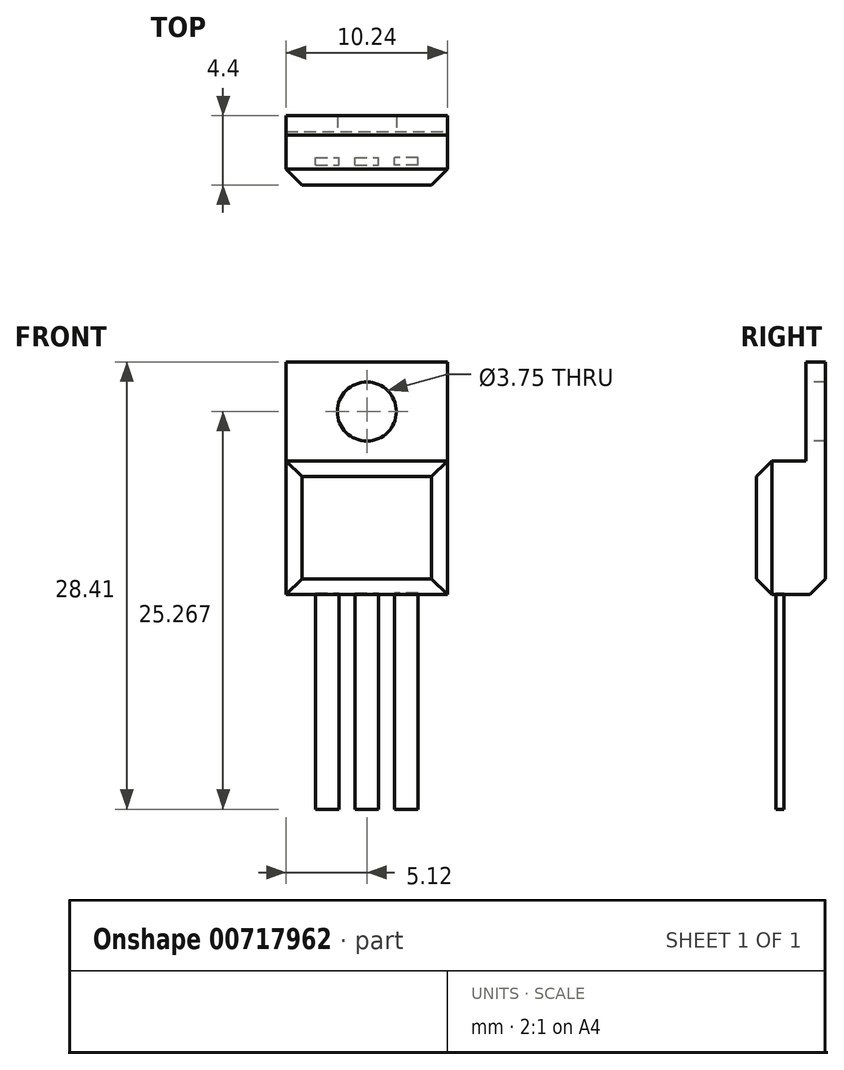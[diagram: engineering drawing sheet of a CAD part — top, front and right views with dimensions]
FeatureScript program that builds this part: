
annotation { "Feature Type Name" : "Feature", "Feature Type Description" : "" }
export const myFeature = defineFeature(function(context is Context, id is Id, definition is map)
    precondition{}
    {
        {
            var Q0;
            Q0=qCreatedBy(makeId("Front.planeOp"),FACE);
            var sketch = newSketch(context, id + "F0", { "sketchPlane" : qUnion([Q0])});
            skLineSegment(sketch, "E0.bottom", {"start": v(-5.12, 4.25) * mm, "end": v(5.12, 4.25) * mm});
            skLineSegment(sketch, "E0.top", {"start": v(-5.12, -4.25) * mm, "end": v(5.12, -4.25) * mm});
            skLineSegment(sketch, "E0.left", {"start": v(-5.12, 4.25) * mm, "end": v(-5.12, -4.25) * mm});
            skLineSegment(sketch, "E0.right", {"start": v(5.12, 4.25) * mm, "end": v(5.12, -4.25) * mm});
            skSolve(sketch);
        }
        {
            var Q0;
            Q0 = qSketchRegion(id + "F0", true);
            extrude(context, id + "F1", {"entities" : qUnion([Q0]), "depth" : 4.4 * mm, "offsetDistance" : 25 * mm});
        }
        {
            var Q0;
            Q0=qCreatedBy(makeId("Front.planeOp"),FACE);
            var sketch = newSketch(context, id + "F2", { "sketchPlane" : qUnion([Q0])});
            skLineSegment(sketch, "E1.bottom", {"start": v(-5.12, 4.12) * mm, "end": v(5.13, 4.13) * mm});
            skLineSegment(sketch, "E1.top", {"start": v(-5.12, 10.53) * mm, "end": v(5.12, 10.53) * mm});
            skLineSegment(sketch, "E1.left", {"start": v(-5.12, 4.12) * mm, "end": v(-5.12, 10.53) * mm});
            skLineSegment(sketch, "E1.right", {"start": v(5.13, 4.13) * mm, "end": v(5.12, 10.53) * mm});
            skSolve(sketch);
        }
        {
            var Q0;
            Q0=makeQuery(id+"F2.imprint","IMPRINT",FACE,{"disambiguationData":[TD([[makeQuery(id+"F2.imprint","IMPRINT",EDGE,{"derivedFrom":sQuery(id+"F2.wireOp",EDGE,"E1.bottom")}),1.0]])]});
            extrude(context, id + "F3", {"entities" : qUnion([Q0]), "operationType" : NewBodyOperationType.ADD, "depth" : 1.25 * mm, "offsetDistance" : 25 * mm});
        }
        {
            var Q0;
            Q0=makeQuery(id+"F3.opExtrude","CAP_FACE",FACE,{"disambiguationData":[OSD([sQuery(id+"F2.wireOp",EDGE,"E1.bottom"),sQuery(id+"F2.wireOp",EDGE,"E1.top"),sQuery(id+"F2.wireOp",EDGE,"E1.left"),sQuery(id+"F2.wireOp",EDGE,"E1.right")])],"isStart":false});
            var sketch = newSketch(context, id + "F4", { "sketchPlane" : qUnion([Q0])});
            skPoint(sketch, "E2", {"position": v(0, 7.39) * mm});
            skPoint(sketch, "E2.positionSnap0", {"position": v(5.12, 7.39) * mm});
            skPoint(sketch, "E2.positionSnap1", {"position": v(0, 10.53) * mm});
            skSolve(sketch);
        }
        {
            var Q0;
            Q0=sQuery(id+"F4.wireOp",VERTEX,"E2");
            var Q1;
            Q1=makeQuery(id+"F1.opExtrude","SWEPT_BODY",BODY,{"disambiguationData":[OSD([sQuery(id+"F0.wireOp",EDGE,"E0.bottom"),sQuery(id+"F0.wireOp",EDGE,"E0.top"),sQuery(id+"F0.wireOp",EDGE,"E0.left"),sQuery(id+"F0.wireOp",EDGE,"E0.right")])]});
            hole(context, id + "F5", {"style" : HoleStyle.SIMPLE, "endStyle" : HoleEndStyle.THROUGH, "holeDiameter" : 3.75 * mm, "majorDiameter" : 5 * mm, "isTappedThrough" : true, "tappedDepth" : 12 * mm, "tapClearance" : 3, "locations" : qUnion([Q0]), "scope" : qUnion([Q1])});
        }
        {
            var Q0;
            Q0=makeQuery(id+"F1.opExtrude","CAP_FACE",FACE,{"disambiguationData":[OSD([sQuery(id+"F0.wireOp",EDGE,"E0.bottom"),sQuery(id+"F0.wireOp",EDGE,"E0.top"),sQuery(id+"F0.wireOp",EDGE,"E0.left"),sQuery(id+"F0.wireOp",EDGE,"E0.right")])],"isStart":false});
            chamfer(context, id + "F6", {"entities" : qUnion([Q0]), "width" : 1 * mm, "tangentPropagation" : true});
        }
        {
            var Q0;
            Q0=qCreatedBy(makeId("Front.planeOp"),FACE);
            var sketch = newSketch(context, id + "F7", { "sketchPlane" : qUnion([Q0])});
            skLineSegment(sketch, "E3.bottom", {"start": v(-0.75, -4.12) * mm, "end": v(0.75, -4.12) * mm});
            skLineSegment(sketch, "E3.top", {"start": v(-0.75, -17.88) * mm, "end": v(0.75, -17.88) * mm});
            skLineSegment(sketch, "E3.left", {"start": v(-0.75, -4.12) * mm, "end": v(-0.75, -17.88) * mm});
            skLineSegment(sketch, "E3.right", {"start": v(0.75, -4.12) * mm, "end": v(0.75, -17.88) * mm});
            skLineSegment(sketch, "E4.bottom", {"start": v(-3.25, -4.12) * mm, "end": v(-1.75, -4.12) * mm});
            skLineSegment(sketch, "E4.top", {"start": v(-3.25, -17.88) * mm, "end": v(-1.75, -17.88) * mm});
            skLineSegment(sketch, "E4.left", {"start": v(-3.25, -4.12) * mm, "end": v(-3.25, -17.88) * mm});
            skLineSegment(sketch, "E4.right", {"start": v(-1.75, -4.12) * mm, "end": v(-1.75, -17.88) * mm});
            skLineSegment(sketch, "E5", {"start": v(0, -31.18) * mm, "end": v(0, 3.38) * mm, "construction": true});
            skLineSegment(sketch, "E6.MirrorCS", {"start": v(1.75, -4.12) * mm, "end": v(1.75, -17.88) * mm});
            skLineSegment(sketch, "E7.MirrorCS", {"start": v(3.25, -4.12) * mm, "end": v(3.25, -17.88) * mm});
            skLineSegment(sketch, "E8.MirrorCS", {"start": v(3.25, -17.88) * mm, "end": v(1.75, -17.88) * mm});
            skLineSegment(sketch, "E9.MirrorCS", {"start": v(3.25, -4.12) * mm, "end": v(1.75, -4.12) * mm});
            skSolve(sketch);
        }
        {
            var Q0;
            Q0=makeQuery(id+"F7.imprint","IMPRINT",FACE,{"disambiguationData":[TD([[makeQuery(id+"F7.imprint","IMPRINT",EDGE,{"derivedFrom":sQuery(id+"F7.wireOp",EDGE,"E4.bottom")}),-1.0]])]});
            var Q1;
            Q1=makeQuery(id+"F7.imprint","IMPRINT",FACE,{"disambiguationData":[TD([[makeQuery(id+"F7.imprint","IMPRINT",EDGE,{"derivedFrom":sQuery(id+"F7.wireOp",EDGE,"E3.bottom")}),-1.0]])]});
            var Q2;
            Q2=makeQuery(id+"F7.imprint","IMPRINT",FACE,{"disambiguationData":[TD([[makeQuery(id+"F7.imprint","IMPRINT",EDGE,{"derivedFrom":sQuery(id+"F7.wireOp",EDGE,"E6.MirrorCS")}),1.0]])]});
            extrude(context, id + "F8", {"entities" : qUnion([Q0, Q1, Q2]), "depth" : 0.5 * mm, "offsetDistance" : 25 * mm});
        }
        {
            var Q0;
            Q0=makeQuery(id+"F8.opExtrude","SWEPT_BODY",BODY,{"disambiguationData":[OSD([sQuery(id+"F7.wireOp",EDGE,"E4.bottom"),sQuery(id+"F7.wireOp",EDGE,"E4.top"),sQuery(id+"F7.wireOp",EDGE,"E4.left"),sQuery(id+"F7.wireOp",EDGE,"E4.right")])]});
            var Q1;
            Q1=makeQuery(id+"F8.opExtrude","SWEPT_BODY",BODY,{"disambiguationData":[OSD([sQuery(id+"F7.wireOp",EDGE,"E3.bottom"),sQuery(id+"F7.wireOp",EDGE,"E3.top"),sQuery(id+"F7.wireOp",EDGE,"E3.left"),sQuery(id+"F7.wireOp",EDGE,"E3.right")])]});
            var Q2;
            Q2=makeQuery(id+"F8.opExtrude","SWEPT_BODY",BODY,{"disambiguationData":[OSD([sQuery(id+"F7.wireOp",EDGE,"E6.MirrorCS"),sQuery(id+"F7.wireOp",EDGE,"E7.MirrorCS"),sQuery(id+"F7.wireOp",EDGE,"E8.MirrorCS"),sQuery(id+"F7.wireOp",EDGE,"E9.MirrorCS")])]});
            transform(context, id + "F9", {"entities" : qUnion([Q0, Q1, Q2]), "transformType" : TransformType.TRANSLATION_3D, "dx" : 0 * mm, "dy" : -2.65 * mm, "dz" : 0 * mm, "makeCopy" : false});
        }
        {
            var Q0;
            Q0=makeQuery(id+"F1.opExtrude","CAP_EDGE",EDGE,{"disambiguationData":[OSD([sQuery(id+"F0.wireOp",EDGE,"E0.top")])],"isStart":true});
            chamfer(context, id + "F10", {"entities" : qUnion([Q0]), "width" : 1 * mm, "tangentPropagation" : true});
        }
    });
